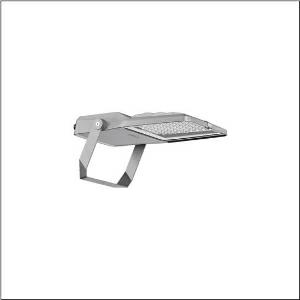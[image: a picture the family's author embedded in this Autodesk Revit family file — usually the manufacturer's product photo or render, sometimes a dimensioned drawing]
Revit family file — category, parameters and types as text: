
# Revit family: floodlight_fl_21_mini___pl61_5xa7775b2c1a_33c0
name_source: partatom
category: Lighting Fixtures
units: mm (PartAtom-declared; Revit-internal decimal feet)

## family parameters
Cut with Voids When Loaded = No
Host = Face
Light Source = No
Part Type = Normal
Room Calculation Point = No
Round Connector Dimension = Use Diameter
Shared = No

## types (1)
- --- (1 x LED, 6110 lm, 45.7 W, 3000K)
    Apparent Load = 46 VA
    CIE Flux Codes = 33 65 98 100 100
    Color Rendering = 70
    Color Temperature = 3000K
    Default Elevation = 1800 mm
    Description = Floodlight FL 21 mini, floodlight, primary light control with lens, of PMMA, primary optical cover: protective disc, of toughened safety glass, transparent, light distribution: PL61, light emission: direct distribution, installation type: surface-mounted, LED, High Power LED, rated luminous flux: 6.110lm, luminous efficacy: 134lm/W, light colour: 730, colour temperature: 3000K, control gear: Smart Interface (Zhaga), control: flexible luminous flux parameterisation, time-dependent luminous flux control, constant luminous flux control, overheat protection, pre-setting: logarithmic dimming characteristic, with terminal, 6-pole, mains connection: 220..240V, AC, 50/60Hz, start of lifetime: 46W, end of service life: 48W, reduction: 22W, luminaire housing, of diecast aluminium, powder-coated, Siteco® metallic grey (DB 702S), corrosivity category C5 mid according to DIN EN ISO 12944, suitable for swimming pools, chlorine-resistant, sealing non-destructively replaceable, mounting bracket, of steel, galvanised, powder-coated, Siteco® metallic grey (DB 702S), Smart Interface above, protection rating (complete): IP66, insulation class (complete): insulation class II (safety insulation), certification: CE, ENEC, VDE, protection symbol: D, impact resistance: IK08, permissible operating ambient temperature: -40..+40°C, permissible operating ambient temperature for outdoor applications: -40..+50°C, standard: DIN EN 12944, LABS conformity tested according to VDMA 24364:2018-05, packaging unit: 1 piece

Light Distribution: PL61
    Height = 70 mm
    Lamp = 1 x LED
    Lamp Light Flux = 6110 lm
    Lamp Power = 45.7 W
    Lamp count = 1
    Length = 485 mm
    Luminous efficacy = 134 lm/W
    Manufacturer = Siteco
    ModVariant = No
    Model = 5XA7775B2C1A
    Number of Poles = 1
    OnlyDefault = Yes
    Power Factor = 1
    Product Name = Floodlight FL 21 mini | PL61
    Product group = floodlight | pylon annexe
    ProductGroupID = 6200
    Protection Class = Protection class II
    Protection Degree = IP 66
    RLX_Detail_Level = 1
    RLX_Emergency_Light_Flux = 0 lm
    RLX_Emergency_Type = 0
    RLX_Emergency_Type_DB = No
    RlxData = <blob elided: 96089 chars, md5=6d5858dd>
    Socket = socket
    Standby Power = 0 W
    System Light Flux = 6110 lm
    System Power = 46 W
    Type Comments = factory setting: luminous flux: 100 % | dim-lin: 254 | 463 mA
    Type Image = l_1006845.jpg
    URL = http://relux.com
    VarID = @adj_172228
    Voltage = 0 V
    Weight = 0.00 kg
    Width = 337 mm

## geometry (parser evidence)
native form markers: Blend x4, Sweep x11
no freeform markers — native parametric forms only
